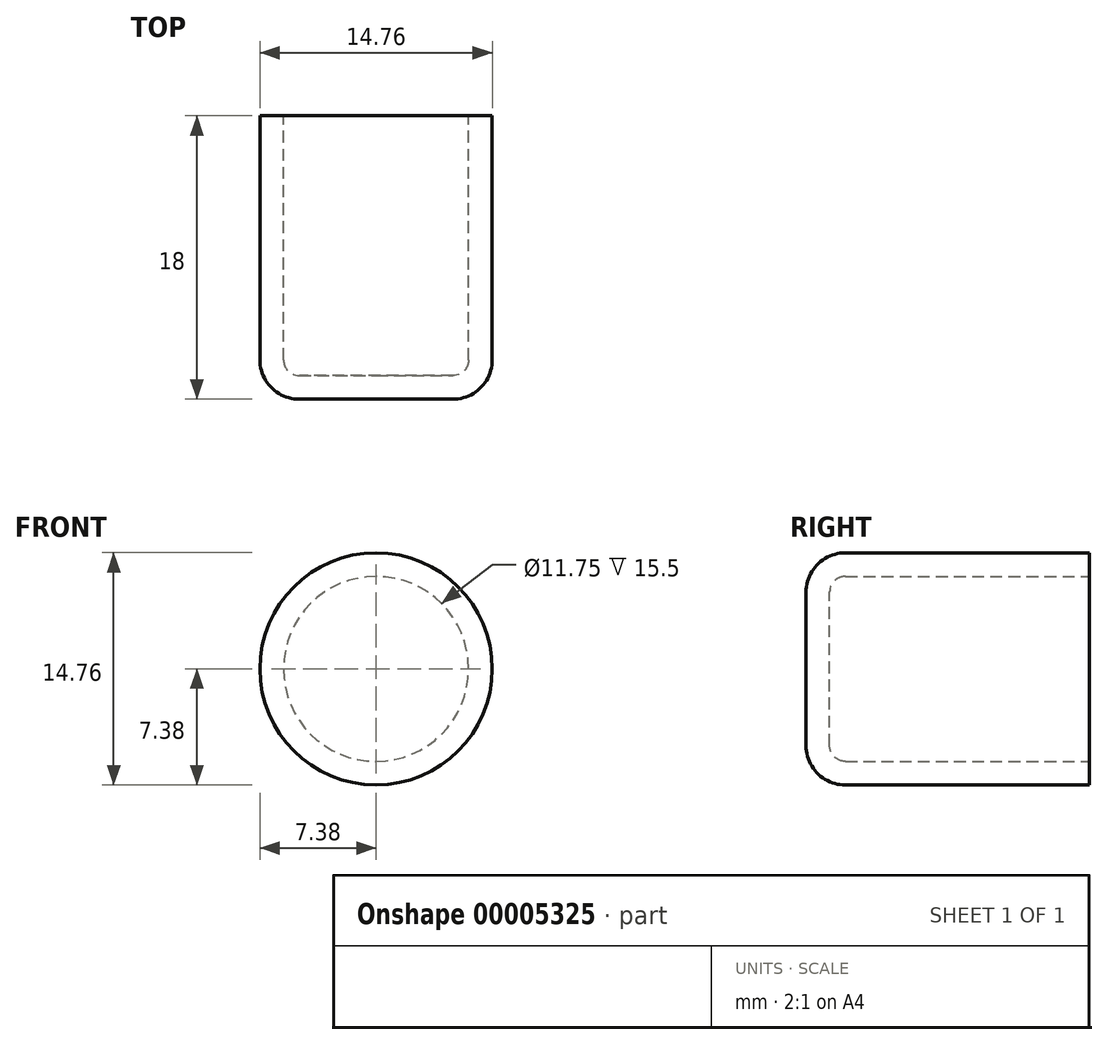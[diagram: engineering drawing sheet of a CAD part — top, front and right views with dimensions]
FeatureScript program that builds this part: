
annotation { "Feature Type Name" : "Feature", "Feature Type Description" : "" }
export const myFeature = defineFeature(function(context is Context, id is Id, definition is map)
    precondition{}
    {
        {
            var Q0;
            Q0=qCreatedBy(makeId("Front.planeOp"),FACE);
            var sketch = newSketch(context, id + "F0", { "sketchPlane" : qUnion([Q0])});
            skCircle(sketch, "E0", {"center": v(0, 0) * mm, "radius": 7.38 * mm});
            skCircle(sketch, "E1", {"center": v(0, 0) * mm, "radius": 6 * mm});
            skSolve(sketch);
        }
        {
            var Q0;
            Q0=makeQuery(id+"F0.imprint","IMPRINT",FACE,{"disambiguationData":[TD([[makeQuery(id+"F0.imprint","IMPRINT",EDGE,{"derivedFrom":sQuery(id+"F0.wireOp",EDGE,"E1")}),1.0]])]});
            var Q1;
            Q1=makeQuery(id+"F0.imprint","IMPRINT",FACE,{"disambiguationData":[TD([[makeQuery(id+"F0.imprint","IMPRINT",EDGE,{"derivedFrom":sQuery(id+"F0.wireOp",EDGE,"E0")}),1.0]])]});
            extrude(context, id + "F1", {"entities" : qUnion([Q0, Q1]), "depth" : 18 * mm});
        }
        {
            var Q0;
            Q0=makeQuery(id+"F1.opExtrude","CAP_EDGE",EDGE,{"disambiguationData":[OSD([sQuery(id+"F0.wireOp",EDGE,"E0")])],"isStart":false});
            fillet(context, id + "F2", {"entities" : qUnion([Q0]), "radius" : 2.5 * mm, "tangentPropagation" : true, "allowEdgeOverflow" : false});
        }
        {
            var Q0;
            Q0=makeQuery(id+"F1.opExtrude","CAP_FACE",FACE,{"disambiguationData":[OSD([sQuery(id+"F0.wireOp",EDGE,"E0")])],"isStart":true});
            shell(context, id + "F3", {"entities" : qUnion([Q0]), "thickness" : 1.5 * mm});
        }
    });
